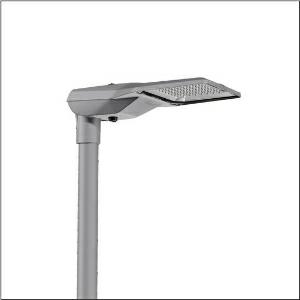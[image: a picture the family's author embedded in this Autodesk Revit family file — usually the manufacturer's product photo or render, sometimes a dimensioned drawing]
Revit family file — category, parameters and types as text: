
# Revit family: streetlight_sl_21_midi___pc-r_5xe3g43t08mb_6611
name_source: partatom
category: Lighting Fixtures
units: mm (PartAtom-declared; Revit-internal decimal feet)

## family parameters
Cut with Voids When Loaded = No
Host = Face
Light Source = No
Part Type = Normal
Room Calculation Point = No
Round Connector Dimension = Use Diameter
Shared = No

## types (1)
- --- (1 x LED, 19200 lm, 147 W, 4000K)
    Apparent Load = 147 VA
    CIE Flux Codes = 38 78 98 100 100
    Color Rendering = 70
    Color Temperature = 4000K
    Default Elevation = 1800 mm
    Description = Streetlight SL 21 midi, mast luminaire, primary light control with lens, of PMMA, primary optical cover: cover, of toughened safety glass, transparent, light distribution: PC-R, light emission: direct distribution, primary light characteristic: asymmetric, right, installation type: side-entry, post-top, LED, High Power LED, rated luminous flux: 19.200lm, luminous efficacy: 131lm/W, light colour: 740, colour temperature: 4000K, control gear: D4i, control: overheat protection, constant luminous flux control, time-dependent luminous flux control, flexible luminous flux parameterisation, pre-setting: logarithmic dimming characteristic, mains connection: 230..240V, AC, 50/60Hz, start of lifetime: 147W, end of service life: 155W, reduction: 65W, luminaire housing, of diecast aluminium, powder-coated, Siteco® metallic grey (DB 702S), corrosivity category C5 mid according to DIN EN ISO 12944, please order mast flange separately, inclination adjustable: 0°, 5°, 10°, 15°, sealing non-destructively replaceable, multi-level sealing system, length: 644mm, width: 335mm, height: 110mm, mast flange for spigot size: 42mm (side-entry): 5XC10008XM4, 60/48mm (side-entry/post-top): 5XC10108XM2, 76/60mm (side-entry/post-top): 5XC10108XM1, mounting height: 4..8m, Smart Interface below and above, protection rating (complete): IP66, insulation class (complete): insulation class II (safety insulation), certification: CE, ENEC, ENEC+, VDE, impact resistance: IK10, permissible operating ambient temperature for outdoor applications: -40..+50°C, standard-compliant lighting for roads and squares, packaging unit: 1 piece

Light Distribution: PC-R
    Height = 111 mm
    Lamp = 1 x LED
    Lamp Light Flux = 19200 lm
    Lamp Power = 147 W
    Lamp count = 1
    Length = 644 mm
    Luminous efficacy = 131 lm/W
    Manufacturer = Siteco
    ModVariant = No
    Model = 5XE3G43T08MB
    Number of Poles = 1
    OnlyDefault = Yes
    Power Factor = 1
    Product Name = Streetlight SL 21 midi | PC-R
    Product group = mast luminaire | pylon top
    ProductGroupID = 6100
    Protection Class = Protection class II
    Protection Degree = IP 66
    RLX_Detail_Level = 1
    RLX_Emergency_Light_Flux = 0 lm
    RLX_Emergency_Type = 0
    RLX_Emergency_Type_DB = No
    RlxData = <blob elided: 29521 chars, md5=1239479d>
    Socket = socket
    Standby Power = 0 W
    System Light Flux = 19200 lm
    System Power = 147 W
    Type Comments = factory setting: luminous flux: 100 % | dim-lin: 254 | 750 mA
    Type Image = l_1004304.jpg
    URL = http://relux.com
    VarID = @adj_085345
    Voltage = 0 V
    Weight = 0.00 kg
    Width = 336 mm

## geometry (parser evidence)
native form markers: Blend x4, Sweep x11
no freeform markers — native parametric forms only
